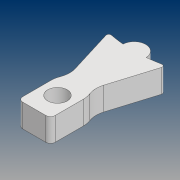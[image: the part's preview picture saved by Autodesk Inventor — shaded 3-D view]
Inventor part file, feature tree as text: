
AUTODESK INVENTOR PART (.ipt)
format: ipt  version: 2021 (Build 250183000, 183)  size: 126,464 bytes
history: native  units: mm
features: fillet x3, extrude x1, sketch x1
ambient origin geometry x8: Origin, YZ Plane, XZ Plane, XY Plane, X Axis, Y Axis, Z Axis, Center Point
bodies: Solid1 (feature_tree)
feature tree (5):
  extrude  "Extrusion1"  Depth=1.0mm
  fillet  "Fillet2"  Radius=5.0mm
  fillet  "Fillet4"  Radius=10.0mm
  fillet  "Fillet5"  Radius=16.5mm
  sketch  "Sketch1"  dims[d1=2.5mm d2=4.2mm d3=5.0mm d4=0.0mm d6=10.0mm d7=16.5mm d8=44.0mm d9=2.96706mm d10=0.5mm d12=10.0mm d13=7.0mm d14=4.75mm d15=1.0mm]
